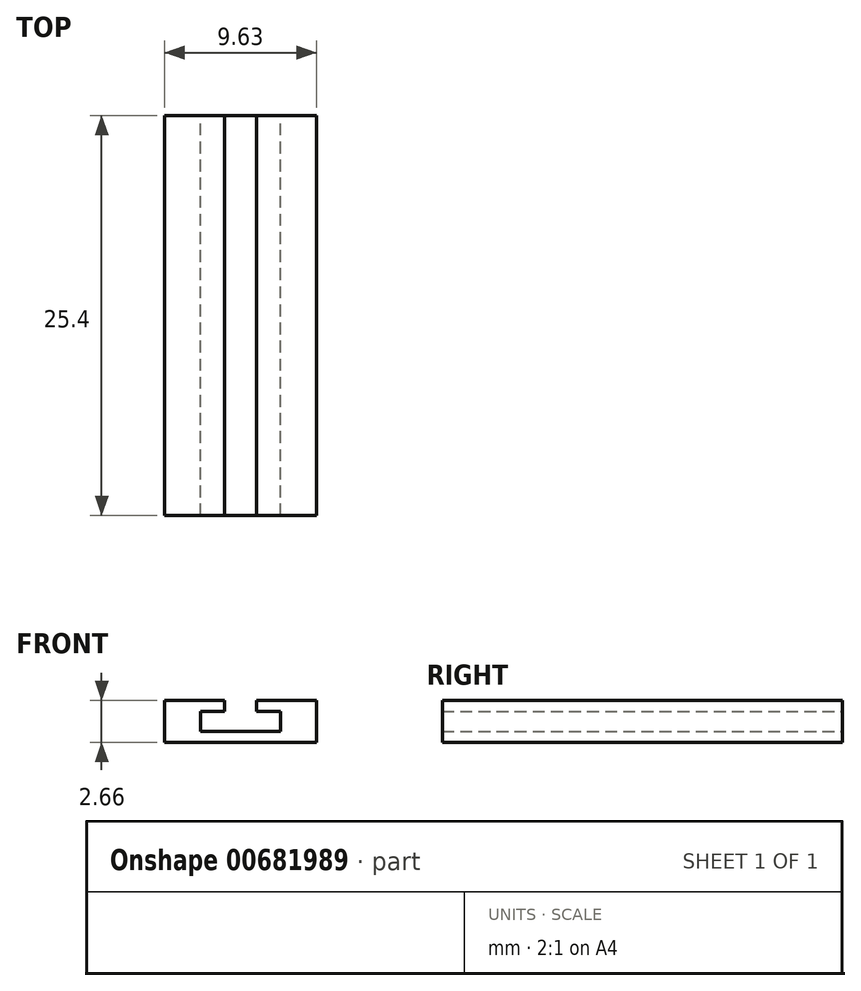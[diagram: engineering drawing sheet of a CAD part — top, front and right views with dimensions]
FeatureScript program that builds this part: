
annotation { "Feature Type Name" : "Feature", "Feature Type Description" : "" }
export const myFeature = defineFeature(function(context is Context, id is Id, definition is map)
    precondition{}
    {
        {
            var Q0;
            Q0=qCreatedBy(makeId("Front.planeOp"),FACE);
            var sketch = newSketch(context, id + "F0", { "sketchPlane" : qUnion([Q0])});
            skLineSegment(sketch, "E0", {"start": v(3.33, -1.16) * mm, "end": v(7.14, -1.16) * mm});
            skLineSegment(sketch, "E1", {"start": v(7.14, -1.16) * mm, "end": v(7.14, -1.86) * mm});
            skLineSegment(sketch, "E2", {"start": v(7.14, -1.86) * mm, "end": v(5.62, -1.86) * mm});
            skLineSegment(sketch, "E3", {"start": v(3.35, -1.16) * mm, "end": v(3.35, -3.82) * mm});
            skLineSegment(sketch, "E4", {"start": v(5.62, -1.86) * mm, "end": v(5.62, -3.13) * mm});
            skLineSegment(sketch, "E5", {"start": v(5.62, -3.13) * mm, "end": v(10.7, -3.13) * mm});
            skLineSegment(sketch, "E6", {"start": v(3.35, -3.82) * mm, "end": v(12.98, -3.82) * mm});
            skLineSegment(sketch, "E7", {"start": v(10.7, -3.13) * mm, "end": v(10.7, -1.86) * mm});
            skLineSegment(sketch, "E8", {"start": v(10.7, -1.86) * mm, "end": v(9.17, -1.86) * mm});
            skLineSegment(sketch, "E9", {"start": v(9.17, -1.86) * mm, "end": v(9.17, -1.16) * mm});
            skLineSegment(sketch, "E10", {"start": v(9.17, -1.16) * mm, "end": v(12.98, -1.16) * mm});
            skLineSegment(sketch, "E11", {"start": v(12.98, -1.16) * mm, "end": v(12.98, -3.82) * mm});
            skSolve(sketch);
        }
        {
            var Q0;
            {var subQ0=sQuery(id+"F0.wireOp",EDGE,"E1");Q0=makeQuery(id+"F0.imprint","IMPRINT",FACE,{"disambiguationData":[TD([[makeQuery(id+"F0.imprint","IMPRINT",EDGE,{"derivedFrom":subQ0}),-1.0]])]});}
            extrude(context, id + "F1", {"entities" : qUnion([Q0]), "depth" : 25.4 * mm, "offsetDistance" : 25.4 * mm});
        }
    });
